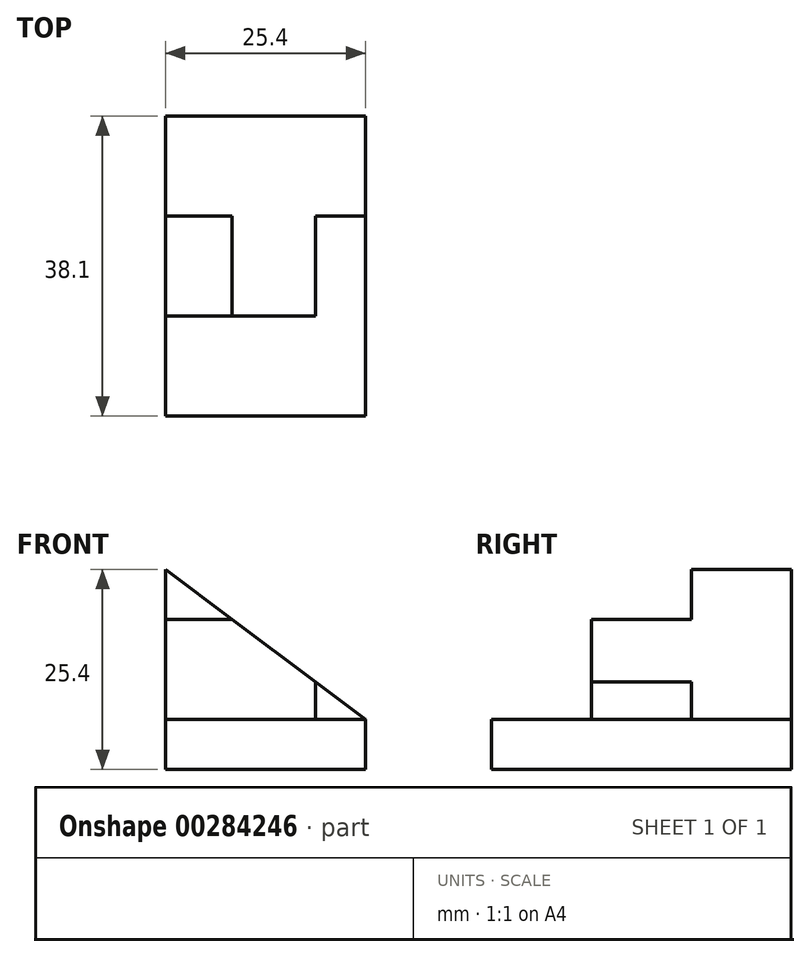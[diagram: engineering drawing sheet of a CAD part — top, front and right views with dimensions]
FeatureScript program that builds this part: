
annotation { "Feature Type Name" : "Feature", "Feature Type Description" : "" }
export const myFeature = defineFeature(function(context is Context, id is Id, definition is map)
    precondition{}
    {
        {
            var Q0;
            Q0=qCreatedBy(makeId("Right.planeOp"),FACE);
            var sketch = newSketch(context, id + "F0", { "sketchPlane" : qUnion([Q0])});
            skLineSegment(sketch, "E0.bottom", {"start": v(-38.1, 0) * mm, "end": v(0, 0) * mm});
            skLineSegment(sketch, "E0.top", {"start": v(-38.1, 6.35) * mm, "end": v(0, 6.35) * mm});
            skLineSegment(sketch, "E0.left", {"start": v(-38.1, 0) * mm, "end": v(-38.1, 6.35) * mm});
            skLineSegment(sketch, "E0.right", {"start": v(0, 0) * mm, "end": v(0, 6.35) * mm});
            skSolve(sketch);
        }
        {
            var Q0;
            Q0 = qSketchRegion(id + "F0", true);
            extrude(context, id + "F1", {"entities" : qUnion([Q0]), "depth" : 25.4 * mm});
        }
        {
            var Q0;
            Q0=qCreatedBy(makeId("Front.planeOp"),FACE);
            var sketch = newSketch(context, id + "F2", { "sketchPlane" : qUnion([Q0])});
            skLineSegment(sketch, "E1", {"start": v(0, 6.35) * mm, "end": v(0, 25.4) * mm});
            skLineSegment(sketch, "E2", {"start": v(0, 25.4) * mm, "end": v(25.4, 6.35) * mm});
            skLineSegment(sketch, "E3", {"start": v(25.4, 6.35) * mm, "end": v(0, 6.35) * mm});
            skSolve(sketch);
        }
        {
            var Q0;
            Q0 = qSketchRegion(id + "F2", true);
            extrude(context, id + "F3", {"entities" : qUnion([Q0]), "operationType" : NewBodyOperationType.ADD, "depth" : 25.4 * mm});
        }
        {
            var Q0;
            Q0=qCreatedBy(makeId("Right.planeOp"),FACE);
            var sketch = newSketch(context, id + "F4", { "sketchPlane" : qUnion([Q0])});
            skLineSegment(sketch, "E4", {"start": v(-25.4, 25.4) * mm, "end": v(-12.7, 25.4) * mm});
            skLineSegment(sketch, "E5", {"start": v(-12.7, 25.4) * mm, "end": v(-12.7, 19.05) * mm});
            skLineSegment(sketch, "E6", {"start": v(-12.7, 19.05) * mm, "end": v(-25.4, 19.05) * mm});
            skLineSegment(sketch, "E7", {"start": v(-25.4, 25.4) * mm, "end": v(-25.4, 19.05) * mm});
            skSolve(sketch);
        }
        {
            var Q0;
            Q0 = qSketchRegion(id + "F4", true);
            extrude(context, id + "F5", {"entities" : qUnion([Q0]), "operationType" : NewBodyOperationType.REMOVE, "endBound" : BoundingType.THROUGH_ALL, "depth" : 52.83 * mm});
        }
        {
            var Q0;
            Q0=makeQuery(id+"F1.opExtrude","SWEPT_FACE",FACE,{"disambiguationData":[OSD([sQuery(id+"F0.wireOp",EDGE,"E0.top")])]});
            var sketch = newSketch(context, id + "F6", { "sketchPlane" : qUnion([Q0])});
            skLineSegment(sketch, "E8", {"start": v(19.05, -12.7) * mm, "end": v(25.4, -12.7) * mm});
            skLineSegment(sketch, "E9", {"start": v(25.4, -12.7) * mm, "end": v(25.4, -25.4) * mm});
            skLineSegment(sketch, "E10", {"start": v(25.4, -25.4) * mm, "end": v(19.05, -25.4) * mm});
            skLineSegment(sketch, "E11", {"start": v(19.05, -25.4) * mm, "end": v(19.05, -12.7) * mm});
            skSolve(sketch);
        }
        {
            var Q0;
            Q0 = qSketchRegion(id + "F6", true);
            extrude(context, id + "F7", {"entities" : qUnion([Q0]), "operationType" : NewBodyOperationType.REMOVE, "endBound" : BoundingType.THROUGH_ALL, "depth" : 25.4 * mm});
        }
    });
